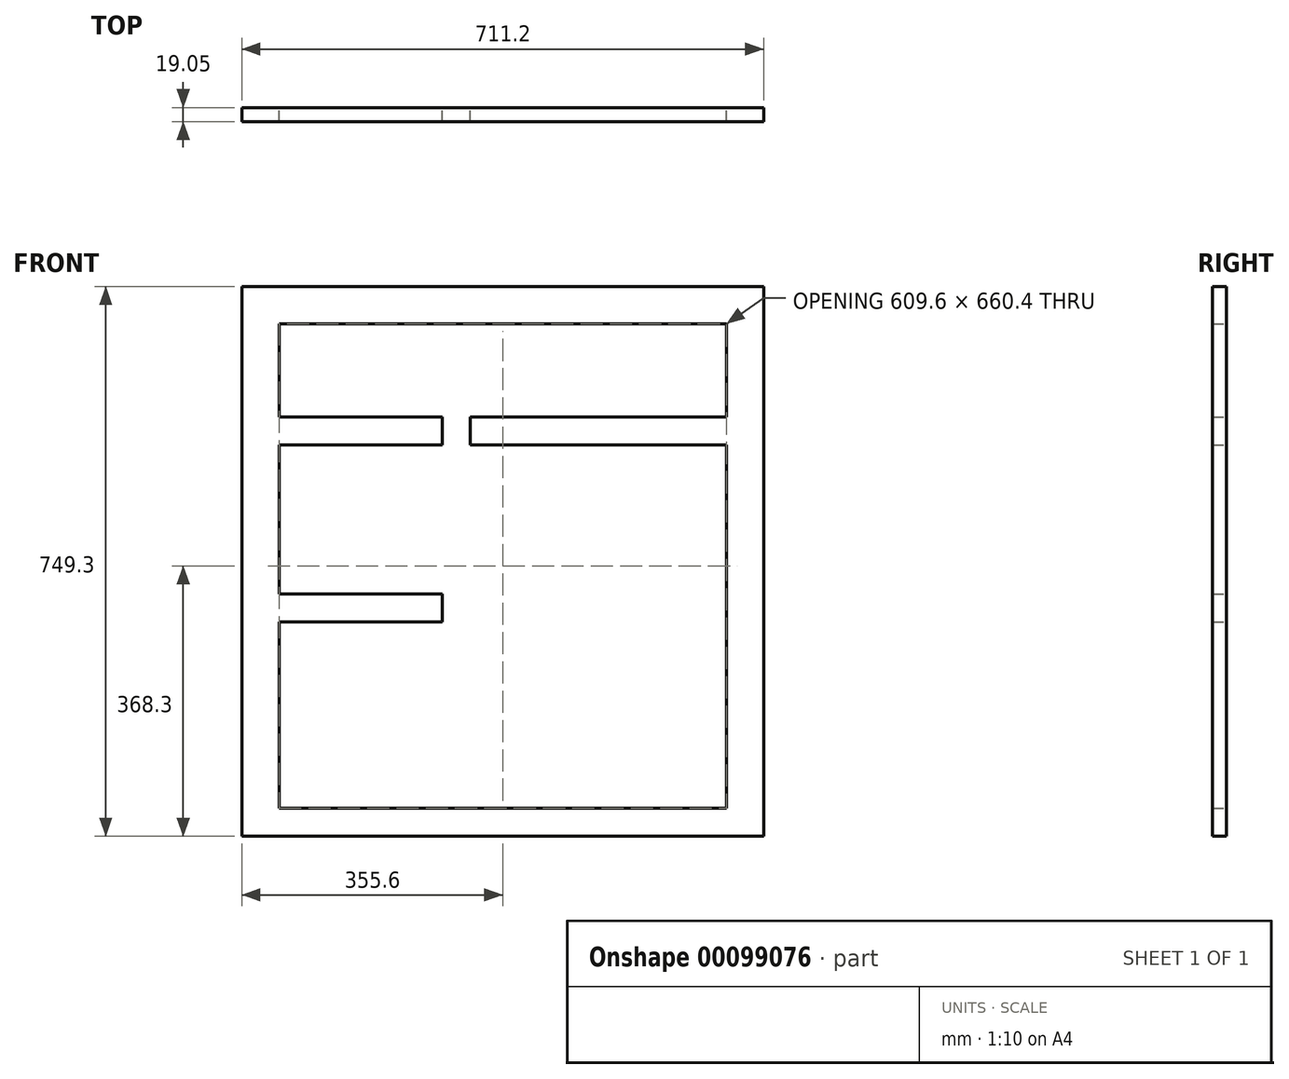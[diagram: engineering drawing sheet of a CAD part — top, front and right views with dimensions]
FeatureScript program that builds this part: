
annotation { "Feature Type Name" : "Feature", "Feature Type Description" : "" }
export const myFeature = defineFeature(function(context is Context, id is Id, definition is map)
    precondition{}
    {
        {
            var Q0;
            Q0=qCreatedBy(makeId("Front.planeOp"),FACE);
            var sketch = newSketch(context, id + "F0", { "sketchPlane" : qUnion([Q0])});
            skLineSegment(sketch, "E0.bottom", {"start": v(0, 0) * mm, "end": v(50.8, 0) * mm});
            skLineSegment(sketch, "E0.top", {"start": v(0, 749.3) * mm, "end": v(50.8, 749.3) * mm});
            skLineSegment(sketch, "E0.left", {"start": v(0, 0) * mm, "end": v(0, 749.3) * mm});
            skLineSegment(sketch, "E0.right", {"start": v(50.8, 0) * mm, "end": v(50.8, 749.3) * mm});
            skLineSegment(sketch, "E1.bottom", {"start": v(50.8, 749.3) * mm, "end": v(660.4, 749.3) * mm});
            skLineSegment(sketch, "E1.top", {"start": v(50.8, 698.5) * mm, "end": v(660.4, 698.5) * mm});
            skLineSegment(sketch, "E1.left", {"start": v(50.8, 749.3) * mm, "end": v(50.8, 698.5) * mm});
            skLineSegment(sketch, "E1.right", {"start": v(660.4, 749.3) * mm, "end": v(660.4, 698.5) * mm});
            skLineSegment(sketch, "E2.bottom", {"start": v(660.4, 749.3) * mm, "end": v(711.2, 749.3) * mm});
            skLineSegment(sketch, "E2.top", {"start": v(660.4, 0) * mm, "end": v(711.2, 0) * mm});
            skLineSegment(sketch, "E2.left", {"start": v(660.4, 749.3) * mm, "end": v(660.4, 0) * mm});
            skLineSegment(sketch, "E2.right", {"start": v(711.2, 749.3) * mm, "end": v(711.2, 0) * mm});
            skLineSegment(sketch, "E3.bottom", {"start": v(660.4, 0) * mm, "end": v(50.8, 0) * mm});
            skLineSegment(sketch, "E3.top", {"start": v(660.4, 38.1) * mm, "end": v(50.8, 38.1) * mm});
            skLineSegment(sketch, "E3.left", {"start": v(660.4, 0) * mm, "end": v(660.4, 38.1) * mm});
            skLineSegment(sketch, "E3.right", {"start": v(50.8, 0) * mm, "end": v(50.8, 38.1) * mm});
            skLineSegment(sketch, "E4.bottom", {"start": v(273.05, 38.1) * mm, "end": v(311.15, 38.1) * mm});
            skLineSegment(sketch, "E4.top", {"start": v(273.05, 698.5) * mm, "end": v(311.15, 698.5) * mm});
            skLineSegment(sketch, "E4.left", {"start": v(273.05, 38.1) * mm, "end": v(273.05, 698.5) * mm});
            skLineSegment(sketch, "E4.right", {"start": v(311.15, 38.1) * mm, "end": v(311.15, 698.5) * mm});
            skLineSegment(sketch, "E5.bottom", {"start": v(311.15, 571.5) * mm, "end": v(660.4, 571.5) * mm});
            skLineSegment(sketch, "E5.top", {"start": v(311.15, 533.4) * mm, "end": v(660.4, 533.4) * mm});
            skLineSegment(sketch, "E5.left", {"start": v(311.15, 571.5) * mm, "end": v(311.15, 533.4) * mm});
            skLineSegment(sketch, "E5.right", {"start": v(660.4, 571.5) * mm, "end": v(660.4, 533.4) * mm});
            skLineSegment(sketch, "E6.bottom", {"start": v(273.05, 533.4) * mm, "end": v(50.8, 533.4) * mm});
            skLineSegment(sketch, "E6.top", {"start": v(273.05, 571.5) * mm, "end": v(50.8, 571.5) * mm});
            skLineSegment(sketch, "E6.left", {"start": v(273.05, 533.4) * mm, "end": v(273.05, 571.5) * mm});
            skLineSegment(sketch, "E6.right", {"start": v(50.8, 533.4) * mm, "end": v(50.8, 571.5) * mm});
            skLineSegment(sketch, "E7.bottom", {"start": v(50.8, 330.2) * mm, "end": v(273.05, 330.2) * mm});
            skLineSegment(sketch, "E7.top", {"start": v(50.8, 292.1) * mm, "end": v(273.05, 292.1) * mm});
            skLineSegment(sketch, "E7.left", {"start": v(50.8, 330.2) * mm, "end": v(50.8, 292.1) * mm});
            skLineSegment(sketch, "E7.right", {"start": v(273.05, 330.2) * mm, "end": v(273.05, 292.1) * mm});
            skSolve(sketch);
        }
        {
            var Q0;
            Q0=makeQuery(id+"F0.imprint","IMPRINT",FACE,{"disambiguationData":[TD([[makeQuery(id+"F0.imprint","IMPRINT",EDGE,{"derivedFrom":sQuery(id+"F0.wireOp",EDGE,"E0.bottom")}),1.0]])]});
            var Q1;
            {var subQ5=sQuery(id+"F0.wireOp",EDGE,"E1.bottom");Q1=makeQuery(id+"F0.imprint","IMPRINT",FACE,{"disambiguationData":[TD([[makeQuery(id+"F0.imprint","IMPRINT",EDGE,{"derivedFrom":subQ5}),-1.0]])]});}
            var Q2;
            {var subQ3=sQuery(id+"F0.wireOp",EDGE,"E2.bottom");Q2=makeQuery(id+"F0.imprint","IMPRINT",FACE,{"disambiguationData":[TD([[makeQuery(id+"F0.imprint","IMPRINT",EDGE,{"derivedFrom":subQ3}),-1.0]])]});}
            var Q3;
            {var subQ3=sQuery(id+"F0.wireOp",EDGE,"E4.bottom");Q3=makeQuery(id+"F0.imprint","IMPRINT",FACE,{"disambiguationData":[TD([[makeQuery(id+"F0.imprint","IMPRINT",EDGE,{"derivedFrom":subQ3}),1.0]])]});}
            var Q4;
            Q4=makeQuery(id+"F0.imprint","IMPRINT",FACE,{"disambiguationData":[TD([[makeQuery(id+"F0.imprint","IMPRINT",EDGE,{"derivedFrom":sQuery(id+"F0.wireOp",EDGE,"E5.bottom")}),-1.0]])]});
            var Q5;
            Q5=makeQuery(id+"F0.imprint","IMPRINT",FACE,{"disambiguationData":[TD([[makeQuery(id+"F0.imprint","IMPRINT",EDGE,{"derivedFrom":sQuery(id+"F0.wireOp",EDGE,"E6.bottom")}),-1.0]])]});
            var Q6;
            Q6=makeQuery(id+"F0.imprint","IMPRINT",FACE,{"disambiguationData":[TD([[makeQuery(id+"F0.imprint","IMPRINT",EDGE,{"derivedFrom":sQuery(id+"F0.wireOp",EDGE,"E7.bottom")}),-1.0]])]});
            var Q7;
            Q7=makeQuery(id+"F0.imprint","IMPRINT",FACE,{"disambiguationData":[TD([[makeQuery(id+"F0.imprint","IMPRINT",EDGE,{"derivedFrom":sQuery(id+"F0.wireOp",EDGE,"E3.bottom")}),-1.0]])]});
            extrude(context, id + "F1", {"entities" : qUnion([Q0, Q1, Q2, Q3, Q4, Q5, Q6, Q7]), "depth" : 19.05 * mm});
        }
    });
